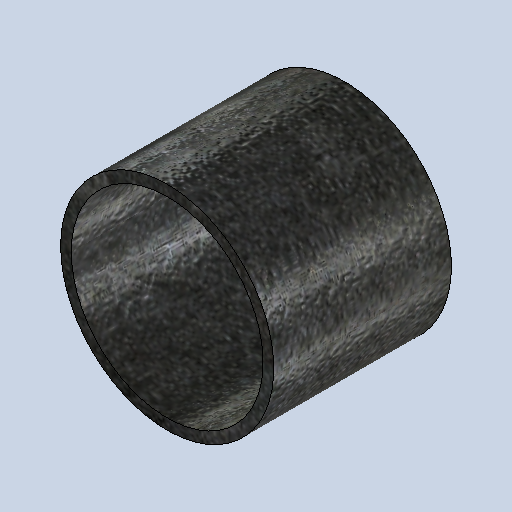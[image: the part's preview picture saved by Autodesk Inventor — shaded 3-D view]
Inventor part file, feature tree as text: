
AUTODESK INVENTOR PART (.ipt)
format: ipt  version: 2025.1 (Build 291241020, 241B)  size: 301,568 bytes
history: native  units: mm
features: extrude x1, sketch x1
ambient origin geometry x8: Origin, YZ Plane, XZ Plane, XY Plane, X Axis, Y Axis, Z Axis, Center Point
bodies: Solid1 (feature_tree)
feature tree (2):
  extrude  "Extrusion1"  Depth=50.0mm
  sketch  "Sketch1"  dims[d0=60.0mm d1=3.0mm d2=50.0mm d3=0.0mm]
